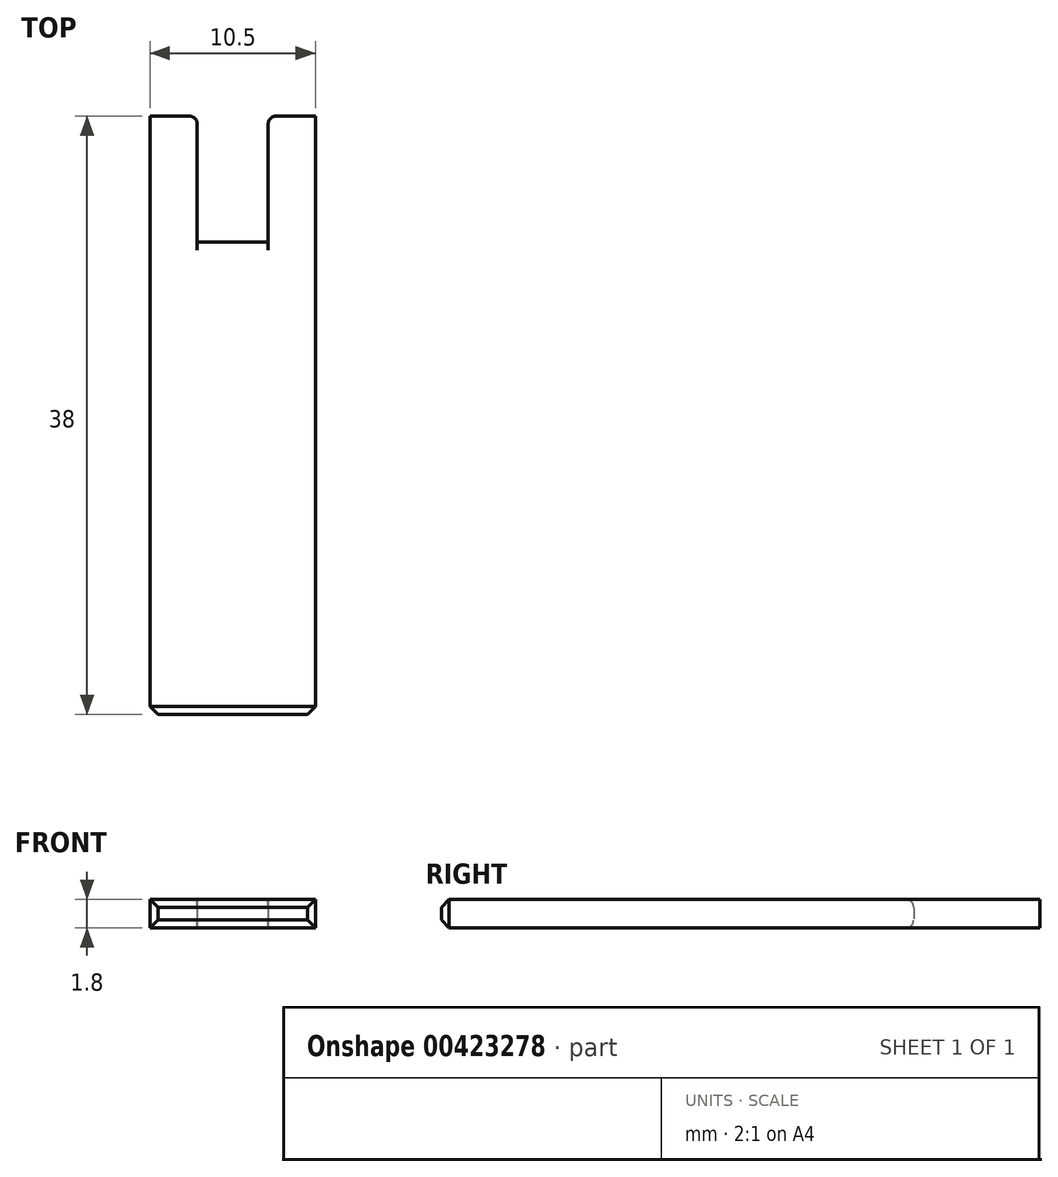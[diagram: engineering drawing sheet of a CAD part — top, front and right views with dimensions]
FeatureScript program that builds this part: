
annotation { "Feature Type Name" : "Feature", "Feature Type Description" : "" }
export const myFeature = defineFeature(function(context is Context, id is Id, definition is map)
    precondition{}
    {
        {
            var Q0;
            Q0=qCreatedBy(makeId("Top.planeOp"),FACE);
            var sketch = newSketch(context, id + "F0", { "sketchPlane" : qUnion([Q0])});
            skLineSegment(sketch, "E0.bottom", {"start": v(5.25, -15) * mm, "end": v(-5.25, -15) * mm});
            skLineSegment(sketch, "E0.top", {"start": v(2.25, 15) * mm, "end": v(-2.25, 15) * mm});
            skLineSegment(sketch, "E0.left", {"start": v(5.25, -15) * mm, "end": v(5.25, 15) * mm});
            skLineSegment(sketch, "E0.right", {"start": v(-5.25, -15) * mm, "end": v(-5.25, 15) * mm});
            skPoint(sketch, "E0.middle", {"position": v(0, 0) * mm});
            skLineSegment(sketch, "E1", {"start": v(0, 0) * mm, "end": v(0, 40.48) * mm, "construction": true});
            skPoint(sketch, "E1.endSnap0", {"position": v(0, 15) * mm});
            skLineSegment(sketch, "E2", {"start": v(-5.25, 15) * mm, "end": v(-5.25, 23) * mm});
            skLineSegment(sketch, "E3", {"start": v(-5.25, 23) * mm, "end": v(-2.25, 23) * mm});
            skLineSegment(sketch, "E4", {"start": v(-2.25, 23) * mm, "end": v(-2.25, 15) * mm});
            skLineSegment(sketch, "E5.MirrorCS", {"start": v(5.25, 23) * mm, "end": v(2.25, 23) * mm});
            skLineSegment(sketch, "E6.MirrorCS", {"start": v(5.25, 15) * mm, "end": v(5.25, 23) * mm});
            skLineSegment(sketch, "E7.MirrorCS", {"start": v(2.25, 23) * mm, "end": v(2.25, 15) * mm});
            skSolve(sketch);
        }
        {
            var Q0;
            Q0 = qSketchRegion(id + "F0", true);
            extrude(context, id + "F1", {"entities" : qUnion([Q0]), "depth" : 1.8 * mm});
        }
        {
            var Q0;
            Q0=makeQuery(id+"F1.opExtrude","SWEPT_EDGE",EDGE,{"disambiguationData":[OSD([sQuery(id+"F0.wireOp",EDGE,"E3"),sQuery(id+"F0.wireOp",EDGE,"E4")])]});
            var Q1;
            Q1=makeQuery(id+"F1.opExtrude","SWEPT_EDGE",EDGE,{"disambiguationData":[OSD([sQuery(id+"F0.wireOp",EDGE,"E5.MirrorCS"),sQuery(id+"F0.wireOp",EDGE,"E7.MirrorCS")])]});
            var Q2;
            Q2=makeQuery(id+"F1.opExtrude","CAP_EDGE",EDGE,{"disambiguationData":[OSD([sQuery(id+"F0.wireOp",EDGE,"E0.top")])],"isStart":false});
            var Q3;
            Q3=makeQuery(id+"F1.opExtrude","CAP_EDGE",EDGE,{"disambiguationData":[OSD([sQuery(id+"F0.wireOp",EDGE,"E0.top")])],"isStart":true});
            fillet(context, id + "F2", {"entities" : qUnion([Q0, Q1, Q2, Q3]), "radius" : 0.5 * mm, "tangentPropagation" : true, "allowEdgeOverflow" : false});
        }
        {
            var Q0;
            Q0=makeQuery(id+"F1.opExtrude","CAP_EDGE",EDGE,{"disambiguationData":[OSD([sQuery(id+"F0.wireOp",EDGE,"E0.bottom")])],"isStart":false});
            var Q1;
            Q1=makeQuery(id+"F1.opExtrude","SWEPT_EDGE",EDGE,{"disambiguationData":[OSD([sQuery(id+"F0.wireOp",EDGE,"E0.bottom"),sQuery(id+"F0.wireOp",EDGE,"E0.left")])]});
            var Q2;
            Q2=makeQuery(id+"F1.opExtrude","CAP_EDGE",EDGE,{"disambiguationData":[OSD([sQuery(id+"F0.wireOp",EDGE,"E0.bottom")])],"isStart":true});
            var Q3;
            Q3=makeQuery(id+"F1.opExtrude","SWEPT_EDGE",EDGE,{"disambiguationData":[OSD([sQuery(id+"F0.wireOp",EDGE,"E0.bottom"),sQuery(id+"F0.wireOp",EDGE,"E0.right")])]});
            chamfer(context, id + "F3", {"entities" : qUnion([Q0, Q1, Q2, Q3]), "width" : 0.5 * mm, "tangentPropagation" : true});
        }
    });
